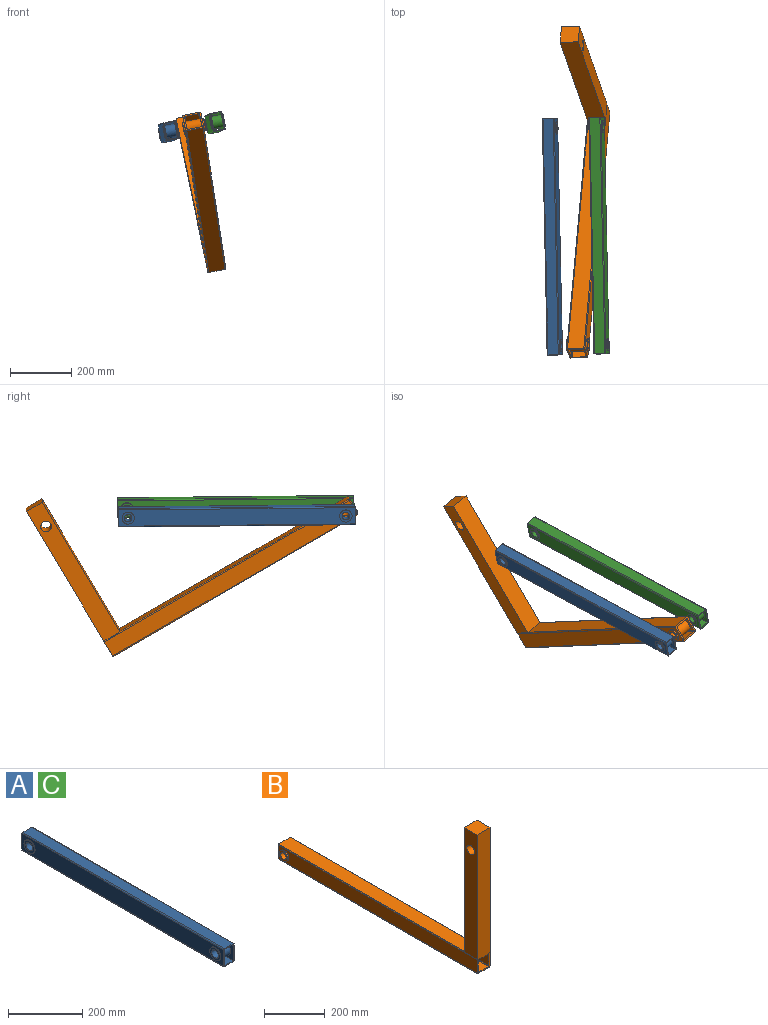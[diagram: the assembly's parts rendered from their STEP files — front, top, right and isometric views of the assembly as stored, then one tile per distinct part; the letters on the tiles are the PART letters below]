
ASSEMBLY  parts=3 mates=2
PART A: 26 faces, bbox 45x770x60 mm
  f0: plane 770x54mm, normal (1,0,0), area 39066.7mm2, adj f1,f11,f12,f13,f18,f23
  f1: cylinder r=3mm len=770mm, axis (0,1,0), area 3628.5mm2, adj f0,f2,f12,f13
  f2: plane 770x34mm, normal (0,0,1), area 26180mm2, adj f1,f3,f12,f13
  f3: cylinder r=3mm len=770mm, axis (0,1,0), area 3628.5mm2, adj f2,f4,f12,f13
  f4: plane 770x54mm, normal (-1,0,0), area 39066.7mm2, adj f3,f5,f12,f13,f16,f21
  f5: cylinder r=3mm len=770mm, axis (0,1,0), area 3628.5mm2, adj f4,f6,f12,f13
  f6: plane 770x34mm, normal (0,0,-1), area 26180mm2, adj f5,f11,f12,f13
  f7: plane 770x54mm, normal (-1,0,0), area 39066.7mm2, adj f8,f10,f12,f13,f14,f20
  f8: plane 770x34mm, normal (0,0,1), area 26180mm2, adj f7,f9,f12,f13
  f9: plane 770x54mm, normal (1,0,0), area 39066.7mm2, adj f8,f10,f12,f13,f14,f20
  f10: plane 770x34mm, normal (0,0,-1), area 26180mm2, adj f7,f9,f12,f13
  f11: cylinder r=3mm len=770mm, axis (0,1,0), area 3628.5mm2, adj f0,f6,f12,f13
  f12: plane 60x40mm, normal (0,-1,0), area 556.3mm2, adj f0,f1,f2,f3,f4,f5,f6,f7
  f13: plane 60x40mm, normal (0,1,0), area 556.3mm2, adj f0,f1,f2,f3,f4,f5,f6,f7
  f14: cylinder r=20mm len=40mm, axis (-1,0,0), area 4272.6mm2, adj f7,f9
  f15: plane 40x40mm, normal (-1,0,0), area 765.8mm2, adj f16,f17
  f16: cylinder r=20mm len=40mm, axis (-1,0,0), area 314.2mm2, adj f4,f15
  f17: cylinder r=12.5mm len=45mm, axis (-1,0,0), area 3534.3mm2, adj f15,f19
  f18: cylinder r=20mm len=40mm, axis (-1,0,0), area 314.2mm2, adj f0,f19
  f19: plane 40x40mm, normal (1,0,0), area 765.8mm2, adj f17,f18
  f20: cylinder r=20mm len=40mm, axis (-1,0,0), area 4272.6mm2, adj f7,f9
  f21: cylinder r=20mm len=40mm, axis (-1,0,0), area 314.2mm2, adj f4,f22
  f22: plane 40x40mm, normal (-1,0,0), area 765.8mm2, adj f21,f24
  f23: cylinder r=20mm len=40mm, axis (-1,0,0), area 314.2mm2, adj f0,f25
  f24: cylinder r=12.5mm len=45mm, axis (-1,0,0), area 3534.3mm2, adj f22,f25
  f25: plane 40x40mm, normal (1,0,0), area 765.8mm2, adj f23,f24
PART B: 31 faces, bbox 70x925x560 mm
  f0: plane 925x54mm, normal (1,0,0), area 48693.4mm2, adj f1,f15,f16,f17,f22
  f1: cylinder r=3mm len=925mm, axis (0,1,0), area 4359mm2, adj f0,f2,f16,f17,f24
  f2: plane 865x54mm, normal (0,0,1), area 46710mm2, adj f1,f3,f17,f27
  f3: cylinder r=3mm len=925mm, axis (0,1,0), area 4359mm2, adj f2,f4,f16,f17,f29
  f4: plane 925x54mm, normal (-1,0,0), area 48693.4mm2, adj f3,f5,f16,f17,f20
  f5: cylinder r=3mm len=925mm, axis (0,1,0), area 4359mm2, adj f4,f6,f16,f17
  f6: plane 925x54mm, normal (0,0,-1), area 49950mm2, adj f5,f15,f16,f17
  f7: cylinder r=3mm len=925mm, axis (0,1,0), area 4359mm2, adj f8,f14,f16,f17
  f8: plane 925x44mm, normal (-1,0,0), area 39443.4mm2, adj f7,f9,f16,f17,f18
  f9: cylinder r=3mm len=925mm, axis (0,1,0), area 4359mm2, adj f8,f10,f16,f17
  f10: plane 925x44mm, normal (0,0,1), area 40700mm2, adj f9,f11,f16,f17
  f11: cylinder r=3mm len=925mm, axis (0,1,0), area 4359mm2, adj f10,f12,f16,f17
  f12: plane 925x44mm, normal (1,0,0), area 39443.4mm2, adj f11,f13,f16,f17,f18
  f13: cylinder r=3mm len=925mm, axis (0,1,0), area 4359mm2, adj f12,f14,f16,f17
  f14: plane 925x44mm, normal (0,0,-1), area 40700mm2, adj f7,f13,f16,f17
  f15: cylinder r=3mm len=925mm, axis (0,1,0), area 4359mm2, adj f0,f6,f16,f17
  f16: plane 560x60mm, normal (0,-1,0), area 31100mm2, adj f0,f1,f3,f4,f5,f6,f7,f8
  f17: plane 60x60mm, normal (0,1,0), area 1100mm2, adj f0,f1,f2,f3,f4,f5,f6,f7
  f18: cylinder r=20mm len=50mm, axis (-1,0,0), area 6283.2mm2, adj f8,f12
  f19: plane 40x40mm, normal (-1,0,0), area 765.8mm2, adj f20,f21
  f20: cylinder r=20mm len=40mm, axis (-1,0,0), area 628.3mm2, adj f4,f19
  f21: cylinder r=12.5mm len=70mm, axis (-1,0,0), area 5497.8mm2, adj f19,f23
  f22: cylinder r=20mm len=40mm, axis (-1,0,0), area 628.3mm2, adj f0,f23
  f23: plane 40x40mm, normal (1,0,0), area 765.8mm2, adj f21,f22
  f24: plane 60x3mm, normal (0,0,-1), area 180mm2, adj f1,f16,f26,f27
  f25: plane 500x60mm, normal (-1,0,0), area 29037.9mm2, adj f16,f27,f28,f29,f30
  f26: plane 500x60mm, normal (1,0,0), area 29037.9mm2, adj f16,f24,f27,f28,f30
  f27: plane 500x60mm, normal (0,1,0), area 30000mm2, adj f2,f24,f25,f26,f28,f29
  f28: plane 60x60mm, normal (0,0,1), area 3600mm2, adj f16,f25,f26,f27
  f29: plane 60x3mm, normal (0,0,-1), area 180mm2, adj f3,f16,f25,f27
  f30: cylinder r=17.5mm len=60mm, axis (1,0,0), area 6597.3mm2, adj f25,f26
PART C: same geometry as A
PLACE A rot(axis=(-0.04,-0.99,0.11),11.2deg) t=(79.97,-1654.62,-666.46)mm
PLACE B rot(axis=(-0.1,0.26,0.96),178.4deg) t=(218,-2432.39,-615.69)mm
PLACE C rot(axis=(-0.01,1,0),168.9deg) t=(259.72,-1649.86,-570.07)mm
MATE revolute B.f18 <-> A.f20  axis (-0.98,-0.02,-0.19) through (151.24,-2392.84,-617.81)mm
MATE fastened A.f2 <-> C.f6  axis (-0.19,0.01,0.98) through (96.22,-2038.74,-600)mm
